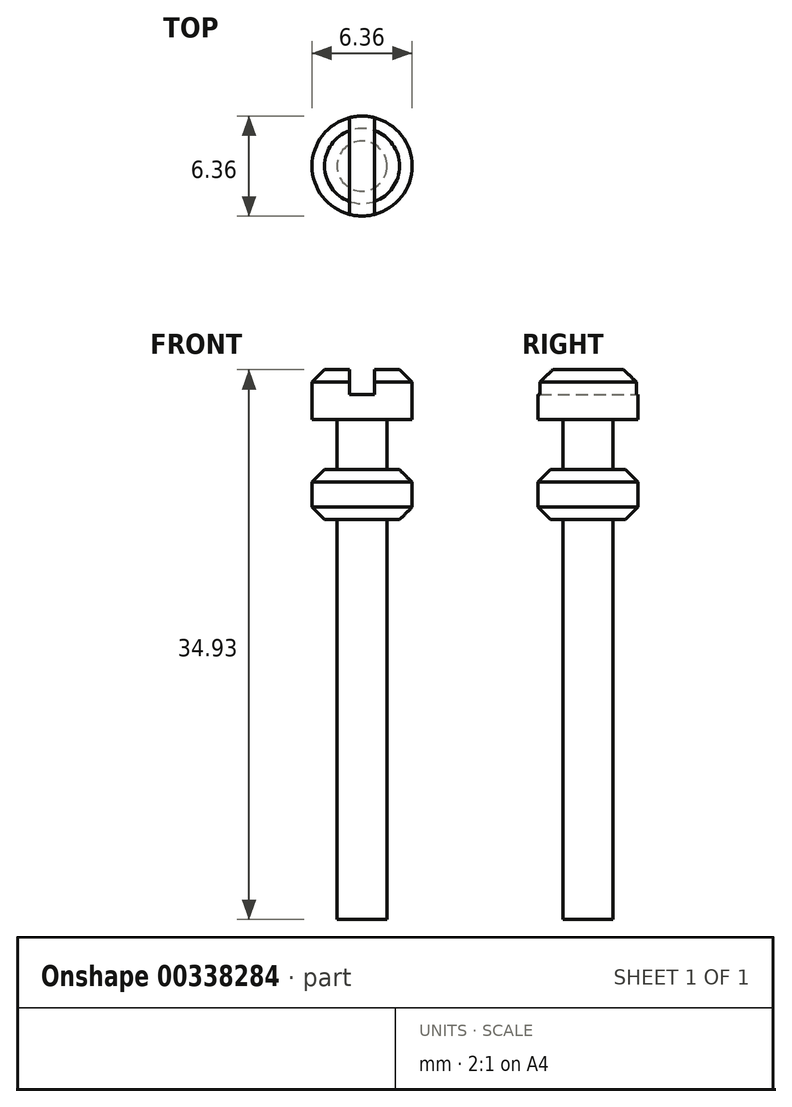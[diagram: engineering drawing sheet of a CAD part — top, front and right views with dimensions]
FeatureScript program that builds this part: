
annotation { "Feature Type Name" : "Feature", "Feature Type Description" : "" }
export const myFeature = defineFeature(function(context is Context, id is Id, definition is map)
    precondition{}
    {
        {
            var Q0;
            Q0=qCreatedBy(makeId("Top.planeOp"),FACE);
            var sketch = newSketch(context, id + "F0", { "sketchPlane" : qUnion([Q0])});
            skCircle(sketch, "E0", {"center": v(0, 0) * mm, "radius": 1.59 * mm});
            skSolve(sketch);
        }
        {
            var Q0;
            Q0 = qSketchRegion(id + "F0", true);
            extrude(context, id + "F1", {"entities" : qUnion([Q0]), "depth" : 25.4 * mm});
        }
        {
            var Q0;
            Q0=makeQuery(id+"F1.opExtrude","CAP_FACE",FACE,{"disambiguationData":[OSD([sQuery(id+"F0.wireOp",EDGE,"E0")])],"isStart":false});
            var sketch = newSketch(context, id + "F2", { "sketchPlane" : qUnion([Q0])});
            skCircle(sketch, "E1", {"center": v(0, 0) * mm, "radius": 3.18 * mm});
            skSolve(sketch);
        }
        {
            var Q0;
            Q0 = qSketchRegion(id + "F2", true);
            extrude(context, id + "F3", {"entities" : qUnion([Q0]), "operationType" : NewBodyOperationType.ADD, "depth" : 3.17 * mm});
        }
        {
            var Q0;
            Q0=makeQuery(id+"F3.opExtrude","CAP_FACE",FACE,{"disambiguationData":[OSD([sQuery(id+"F2.wireOp",EDGE,"E1")])],"isStart":false});
            var sketch = newSketch(context, id + "F4", { "sketchPlane" : qUnion([Q0])});
            skCircle(sketch, "E2", {"center": v(0, 0) * mm, "radius": 1.59 * mm});
            skSolve(sketch);
        }
        {
            var Q0;
            Q0 = qSketchRegion(id + "F4", true);
            extrude(context, id + "F5", {"entities" : qUnion([Q0]), "operationType" : NewBodyOperationType.ADD, "depth" : 3.17 * mm});
        }
        {
            var Q0;
            Q0=makeQuery(id+"F5.opExtrude","CAP_FACE",FACE,{"disambiguationData":[OSD([sQuery(id+"F4.wireOp",EDGE,"E2")])],"isStart":false});
            var sketch = newSketch(context, id + "F6", { "sketchPlane" : qUnion([Q0])});
            skCircle(sketch, "E3", {"center": v(0, 0) * mm, "radius": 3.18 * mm});
            skSolve(sketch);
        }
        {
            var Q0;
            Q0 = qSketchRegion(id + "F6", true);
            extrude(context, id + "F7", {"entities" : qUnion([Q0]), "operationType" : NewBodyOperationType.ADD, "depth" : 3.17 * mm});
        }
        {
            var Q0;
            Q0=makeQuery(id+"F7.opExtrude","CAP_FACE",FACE,{"disambiguationData":[OSD([sQuery(id+"F6.wireOp",EDGE,"E3")])],"isStart":false});
            var sketch = newSketch(context, id + "F8", { "sketchPlane" : qUnion([Q0])});
            skLineSegment(sketch, "E4.bottom", {"start": v(0.8, -3.18) * mm, "end": v(-0.8, -3.18) * mm});
            skLineSegment(sketch, "E4.top", {"start": v(0.8, 3.18) * mm, "end": v(-0.8, 3.18) * mm});
            skLineSegment(sketch, "E4.left", {"start": v(0.8, -3.17) * mm, "end": v(0.8, 3.17) * mm});
            skLineSegment(sketch, "E4.right", {"start": v(-0.8, -3.17) * mm, "end": v(-0.8, 3.17) * mm});
            skPoint(sketch, "E4.middle", {"position": v(0, 0) * mm});
            skSolve(sketch);
        }
        {
            var Q0;
            Q0 = qSketchRegion(id + "F8", true);
            extrude(context, id + "F9", {"entities" : qUnion([Q0]), "operationType" : NewBodyOperationType.REMOVE, "oppositeDirection" : true, "depth" : 1.59 * mm});
        }
        {
            var Q0;
            {var subQ0=sQuery(id+"F6.wireOp",EDGE,"E3");Q0=makeQuery(id+"F9.boolean.opBoolean","SPLIT",EDGE,{"disambiguationData":[TD([makeQuery(id+"F9.opExtrude","SWEPT_FACE",FACE,{"disambiguationData":[OSD([sQuery(id+"F8.wireOp",EDGE,"E4.right")])]})])],"derivedFrom":makeQuery(id+"F7.opExtrude","CAP_EDGE",EDGE,{"disambiguationData":[OSD([subQ0])],"isStart":false})});}
            var Q1;
            {var subQ0=sQuery(id+"F6.wireOp",EDGE,"E3");Q1=makeQuery(id+"F9.boolean.opBoolean","SPLIT",EDGE,{"disambiguationData":[TD([makeQuery(id+"F9.opExtrude","SWEPT_FACE",FACE,{"disambiguationData":[OSD([sQuery(id+"F8.wireOp",EDGE,"E4.left")])]})])],"derivedFrom":makeQuery(id+"F7.opExtrude","CAP_EDGE",EDGE,{"disambiguationData":[OSD([subQ0])],"isStart":false})});}
            var Q2;
            Q2=makeQuery(id+"F3.opExtrude","CAP_EDGE",EDGE,{"disambiguationData":[OSD([sQuery(id+"F2.wireOp",EDGE,"E1")])],"isStart":false});
            var Q3;
            Q3=makeQuery(id+"F3.opExtrude","CAP_EDGE",EDGE,{"disambiguationData":[OSD([sQuery(id+"F2.wireOp",EDGE,"E1")])],"isStart":true});
            chamfer(context, id + "F10", {"entities" : qUnion([Q0, Q1, Q2, Q3]), "width" : 0.8 * mm, "tangentPropagation" : true});
        }
    });
